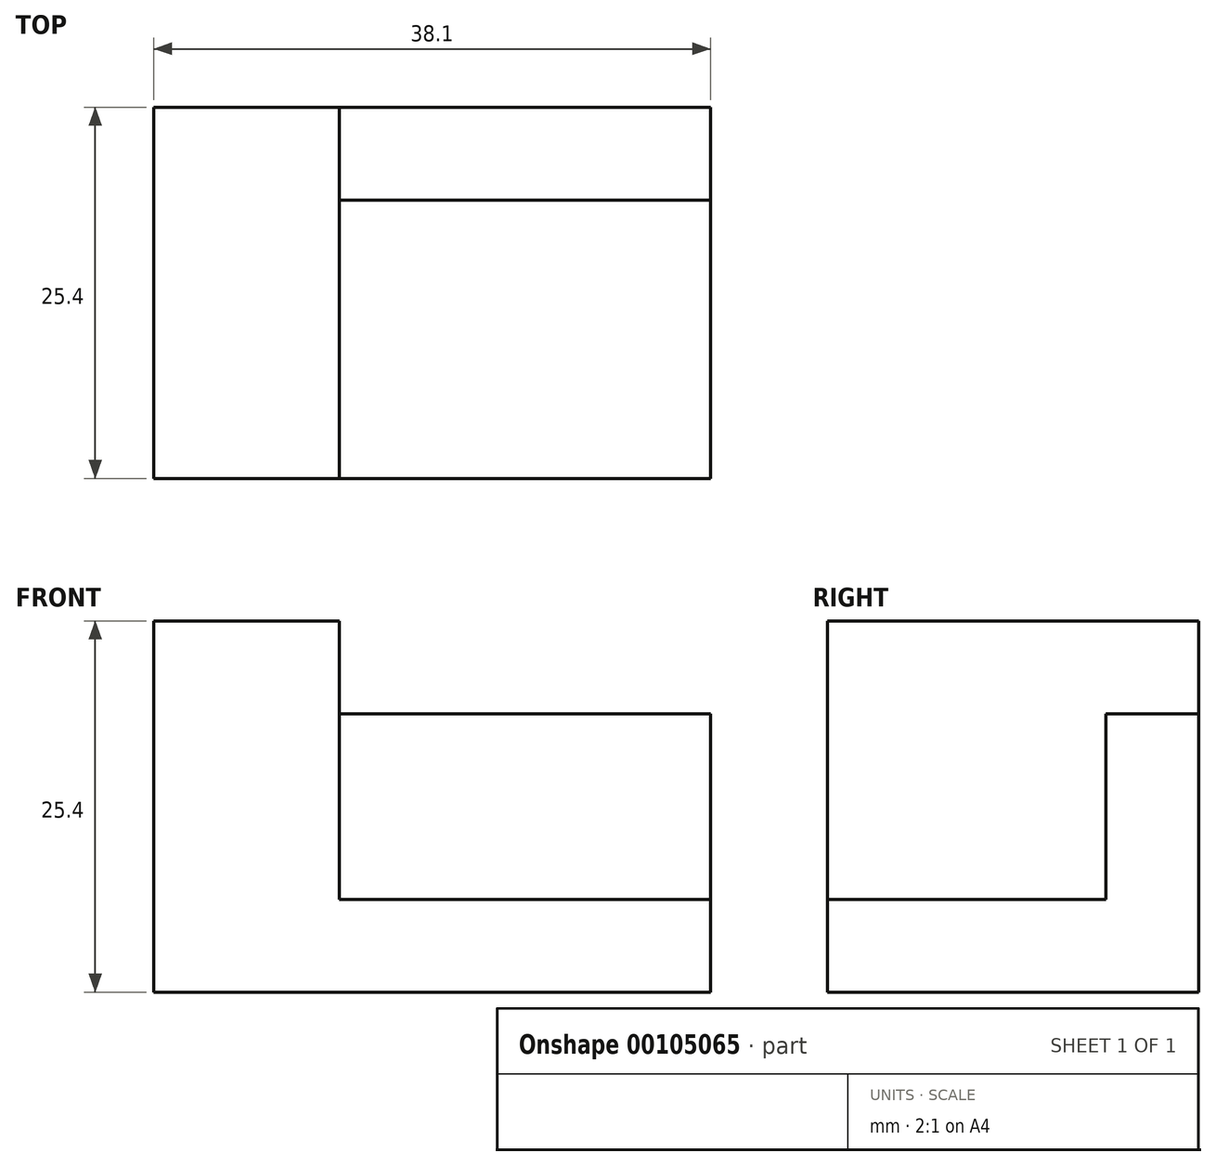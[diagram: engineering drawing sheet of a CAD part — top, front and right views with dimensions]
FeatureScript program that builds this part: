
annotation { "Feature Type Name" : "Feature", "Feature Type Description" : "" }
export const myFeature = defineFeature(function(context is Context, id is Id, definition is map)
    precondition{}
    {
        {
            var Q0;
            Q0=qCreatedBy(makeId("Right.planeOp"),FACE);
            var sketch = newSketch(context, id + "F0", { "sketchPlane" : qUnion([Q0])});
            skLineSegment(sketch, "E0.bottom", {"start": v(0, 0) * mm, "end": v(25.4, 0) * mm});
            skLineSegment(sketch, "E0.top", {"start": v(0, 25.4) * mm, "end": v(25.4, 25.4) * mm});
            skLineSegment(sketch, "E0.left", {"start": v(0, 0) * mm, "end": v(0, 25.4) * mm});
            skLineSegment(sketch, "E0.right", {"start": v(25.4, 0) * mm, "end": v(25.4, 25.4) * mm});
            skLineSegment(sketch, "E1", {"start": v(0, 0) * mm, "end": v(0, 6.35) * mm});
            skLineSegment(sketch, "E2", {"start": v(0, 6.35) * mm, "end": v(19.05, 6.35) * mm});
            skLineSegment(sketch, "E3", {"start": v(19.05, 6.35) * mm, "end": v(19.05, 19.05) * mm});
            skLineSegment(sketch, "E4", {"start": v(19.05, 19.05) * mm, "end": v(25.4, 19.05) * mm});
            skSolve(sketch);
        }
        {
            var Q0;
            Q0=qCreatedBy(makeId("Front.planeOp"),FACE);
            var sketch = newSketch(context, id + "F1", { "sketchPlane" : qUnion([Q0])});
            skLineSegment(sketch, "E5.bottom", {"start": v(0, 0) * mm, "end": v(38.1, 0) * mm});
            skLineSegment(sketch, "E5.top", {"start": v(0, 25.4) * mm, "end": v(12.7, 25.4) * mm});
            skLineSegment(sketch, "E5.left", {"start": v(0, 0) * mm, "end": v(0, 25.4) * mm});
            skLineSegment(sketch, "E5.right", {"start": v(38.1, 0) * mm, "end": v(38.1, 19.05) * mm});
            skLineSegment(sketch, "E6.top", {"start": v(12.7, 6.35) * mm, "end": v(38.1, 6.35) * mm});
            skLineSegment(sketch, "E6.left", {"start": v(12.7, 25.4) * mm, "end": v(12.7, 6.35) * mm});
            skLineSegment(sketch, "E6.right", {"start": v(38.1, 19.05) * mm, "end": v(38.1, 6.35) * mm});
            skLineSegment(sketch, "E7.top", {"start": v(12.7, 19.05) * mm, "end": v(38.1, 19.05) * mm});
            skLineSegment(sketch, "E7.left", {"start": v(12.7, 25.4) * mm, "end": v(12.7, 19.05) * mm});
            skSolve(sketch);
        }
        {
            var Q0;
            {var subQ1=sQuery(id+"F0.wireOp",EDGE,"E0.bottom");Q0=makeQuery(id+"F0.imprint","IMPRINT",FACE,{"disambiguationData":[TD([[makeQuery(id+"F0.imprint","IMPRINT",EDGE,{"derivedFrom":subQ1}),1.0]])]});}
            extrude(context, id + "F2", {"entities" : qUnion([Q0]), "depth" : 38.1 * mm});
        }
        {
            var Q0;
            Q0=makeQuery(id+"F1.imprint","IMPRINT",FACE,{"disambiguationData":[TD([[makeQuery(id+"F1.imprint","IMPRINT",EDGE,{"derivedFrom":sQuery(id+"F1.wireOp",EDGE,"E5.bottom")}),1.0]])]});
            extrude(context, id + "F3", {"entities" : qUnion([Q0]), "operationType" : NewBodyOperationType.ADD, "oppositeDirection" : true, "depth" : 25.4 * mm});
        }
    });
